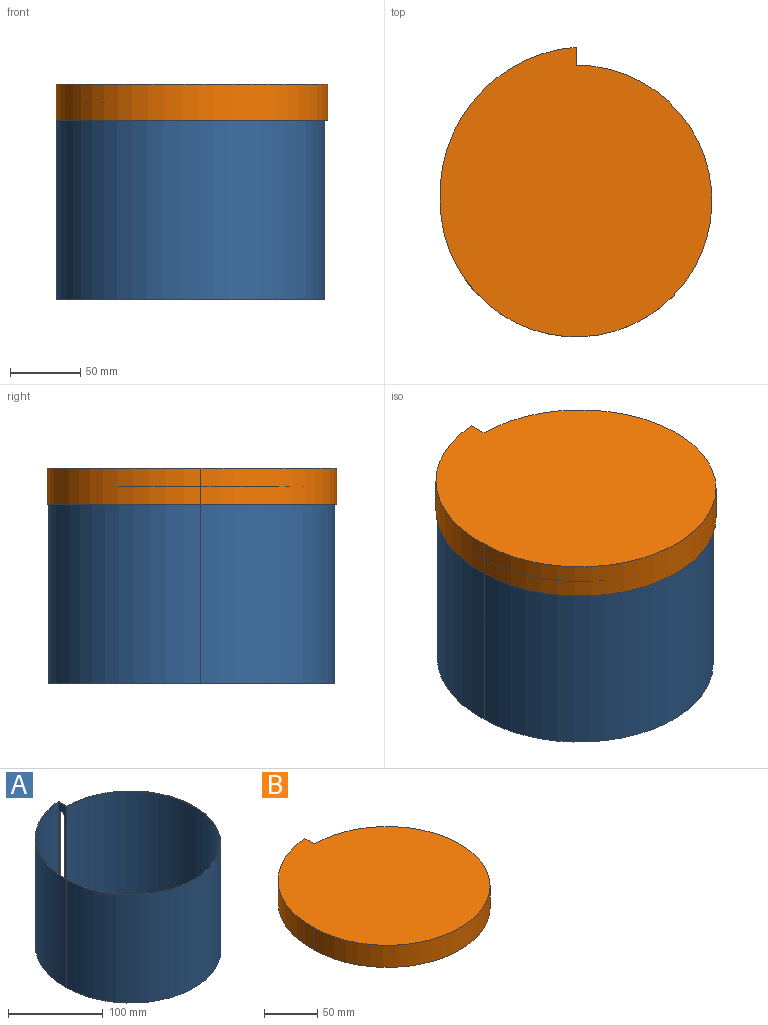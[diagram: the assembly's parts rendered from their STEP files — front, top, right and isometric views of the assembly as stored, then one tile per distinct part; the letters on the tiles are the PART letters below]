
ASSEMBLY  parts=2 mates=1
PART A: 13 faces, bbox 190.6x203.2x139.7 mm
  f0: plane 139.7x12.7mm, normal (1,0,0), area 1016.7mm2, adj f2,f3,f4,f5,f9,f10,f11,f12
  f1: plane 138.7x12.61mm, normal (-1,0,0), area 990.9mm2, adj f2,f6,f7,f8,f9,f10,f11,f12
  f2: plane 203.2x190.56mm, normal (0,0,1), area 617.1mm2, adj f0,f1,f3,f5,f6,f8
  f3: cylinder r=95.25mm len=190.5mm, axis (0,0,-1), area 62705.1mm2, adj f0,f2,f4,f5
  f4: plane 203.2x190.56mm, normal (0,0,-1), area 29354.1mm2, adj f0,f3,f5
  f5: cylinder r=104.72mm len=139.7mm, axis (0,0,-1), area 22174.4mm2, adj f0,f2,f3,f4
  f6: cylinder r=94.25mm len=188.5mm, axis (0,0,-1), area 61743.7mm2, adj f1,f2,f7,f8
  f7: plane 201.1x188.56mm, normal (0,0,1), area 28737mm2, adj f1,f6,f8
  f8: cylinder r=103.72mm len=138.7mm, axis (0,0,-1), area 21656mm2, adj f1,f2,f6,f7
  f9: plane 114.3x1mm, normal (0,-1,0), area 114.3mm2, adj f0,f1,f10,f12
  f10: cylinder r=3.17mm len=6.35mm, axis (1,0,0), area 10mm2, adj f0,f1,f9,f11
  f11: plane 114.3x1mm, normal (0,1,0), area 114.3mm2, adj f0,f1,f10,f12
  f12: cylinder r=3.17mm len=6.35mm, axis (1,0,0), area 10mm2, adj f0,f1,f9,f11
PART B: 9 faces, bbox 193.2x205.7x25.4 mm
  f0: cylinder r=96.52mm len=193.04mm, axis (0,0,-1), area 11552.9mm2, adj f1,f2,f3,f4
  f1: plane 205.74x193.15mm, normal (0,0,1), area 30182.1mm2, adj f0,f3,f4
  f2: plane 205.74x193.15mm, normal (0,0,-1), area 625.6mm2, adj f0,f3,f4,f5,f7,f8
  f3: plane 25.4x12.7mm, normal (1,0,0), area 322.6mm2, adj f0,f1,f2,f4
  f4: cylinder r=104.72mm len=109.22mm, axis (0,0,-1), area 4094.8mm2, adj f0,f1,f2,f3
  f5: cylinder r=95.52mm len=191.04mm, axis (0,0,-1), area 11008.1mm2, adj f2,f6,f7,f8
  f6: plane 203.65x191.15mm, normal (0,0,-1), area 29556.5mm2, adj f5,f7,f8
  f7: plane 24.4x12.62mm, normal (-1,0,0), area 307.9mm2, adj f2,f5,f6,f8
  f8: cylinder r=103.72mm len=108.11mm, axis (0,0,-1), area 3870.2mm2, adj f2,f5,f6,f7
PLACE A at identity
PLACE B t=(1,-0.22,127.5)mm
MATE fastened B.f7 <-> A.f0  axis (-1,0,0) through (0,101.6,139.7)mm
